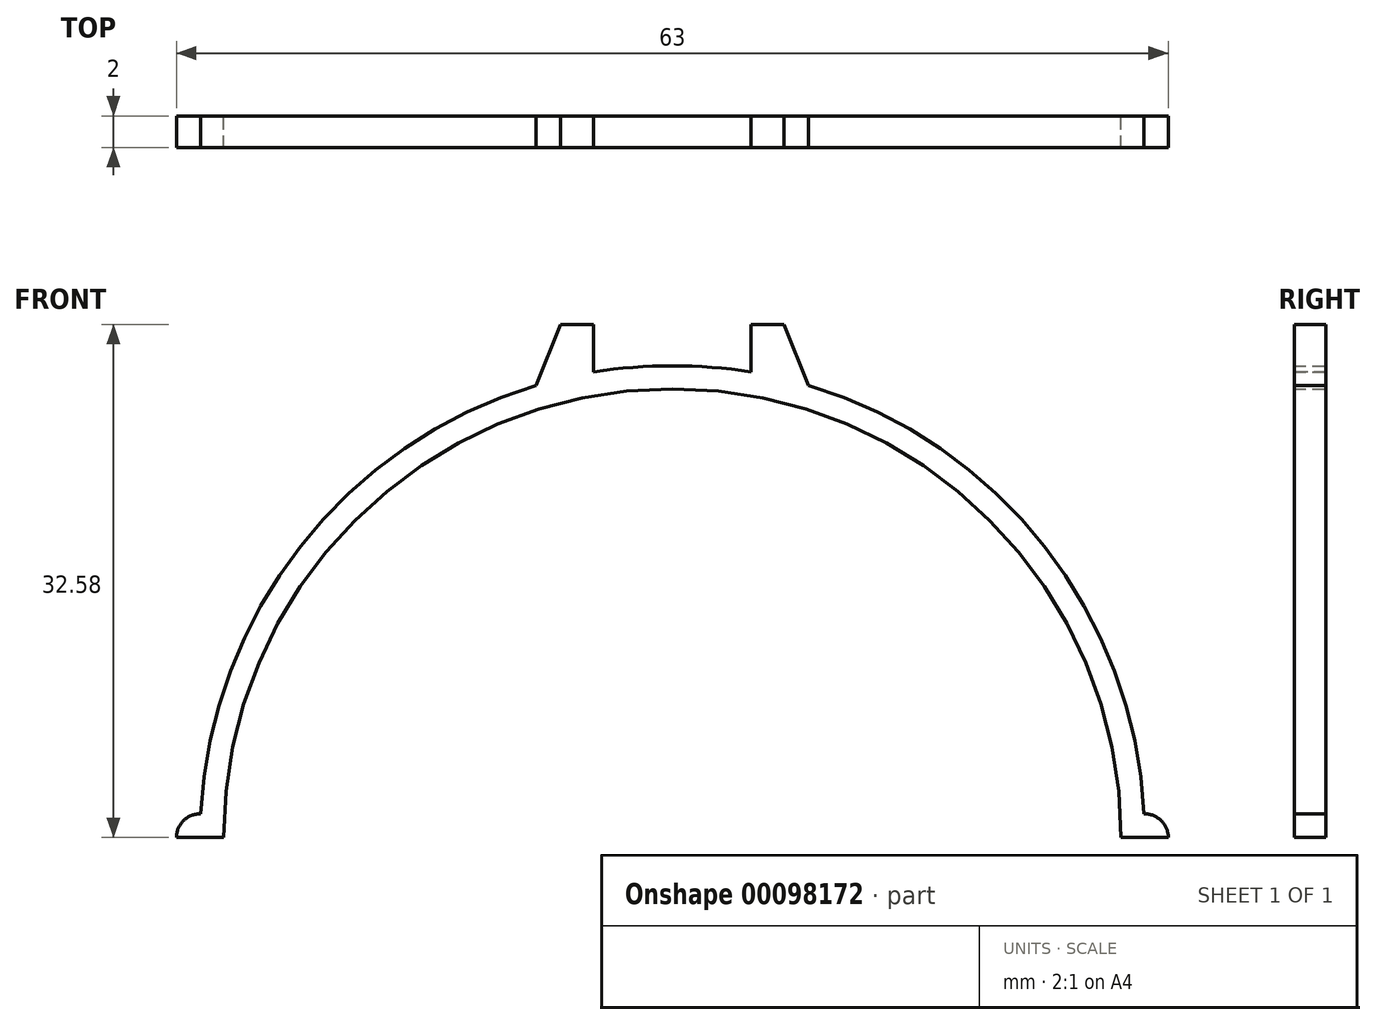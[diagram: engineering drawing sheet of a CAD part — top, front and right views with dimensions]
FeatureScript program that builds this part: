
annotation { "Feature Type Name" : "Feature", "Feature Type Description" : "" }
export const myFeature = defineFeature(function(context is Context, id is Id, definition is map)
    precondition{}
    {
        {
            var Q0;
            Q0=qCreatedBy(makeId("Front.planeOp"),FACE);
            var sketch = newSketch(context, id + "F0", { "sketchPlane" : qUnion([Q0])});
            skArc(sketch, "E0", {"start": v(29.96, 1.5) * mm, "mid": v(23.62, 18.5) * mm, "end": v(8.65, 28.72) * mm});
            skArc(sketch, "E1", {"start": v(28.5, 0) * mm, "mid": v(0, 28.5) * mm, "end": v(-28.5, 0) * mm});
            skLineSegment(sketch, "E2", {"start": v(-30, 0) * mm, "end": v(-28.5, 0) * mm});
            skLineSegment(sketch, "E3", {"start": v(28.5, 0) * mm, "end": v(30, 0) * mm});
            skArc(sketch, "E4", {"start": v(-29.96, 1.5) * mm, "mid": v(-31.05, 1.07) * mm, "end": v(-31.5, 0) * mm});
            skArc(sketch, "E5", {"start": v(31.5, 0) * mm, "mid": v(31.05, 1.07) * mm, "end": v(29.96, 1.5) * mm});
            skLineSegment(sketch, "E6", {"start": v(-31.5, 0) * mm, "end": v(-30, 0) * mm});
            skLineSegment(sketch, "E7", {"start": v(30, 0) * mm, "end": v(31.5, 0) * mm});
            skArc(sketch, "E8.trimOffspring", {"start": v(-8.65, 28.72) * mm, "mid": v(-23.62, 18.5) * mm, "end": v(-29.96, 1.5) * mm});
            skLineSegment(sketch, "E9", {"start": v(-5, 32.58) * mm, "end": v(-5, 29.58) * mm});
            skLineSegment(sketch, "E10", {"start": v(-5, 32.58) * mm, "end": v(-7.1, 32.58) * mm});
            skLineSegment(sketch, "E11", {"start": v(-7.1, 32.58) * mm, "end": v(-8.65, 28.72) * mm});
            skLineSegment(sketch, "E12.MirrorCS", {"start": v(7.1, 32.58) * mm, "end": v(8.65, 28.72) * mm});
            skLineSegment(sketch, "E13.MirrorCS", {"start": v(5, 32.58) * mm, "end": v(7.1, 32.58) * mm});
            skLineSegment(sketch, "E14.MirrorCS", {"start": v(5, 32.58) * mm, "end": v(5, 29.58) * mm});
            skArc(sketch, "E15.trimOffspring", {"start": v(5, 29.58) * mm, "mid": v(5, 29.58) * mm, "end": v(5, 29.58) * mm});
            skArc(sketch, "E16", {"start": v(5, 29.58) * mm, "mid": v(0, 29.96) * mm, "end": v(-5, 29.58) * mm});
            skSolve(sketch);
        }
        {
            var Q0;
            Q0 = qSketchRegion(id + "F0", true);
            extrude(context, id + "F1", {"entities" : qUnion([Q0]), "depth" : 2 * mm});
        }
    });
